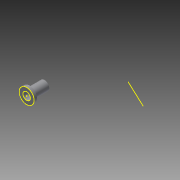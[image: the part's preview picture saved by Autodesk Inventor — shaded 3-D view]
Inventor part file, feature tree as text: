
AUTODESK INVENTOR PART (.ipt)
format: ipt  version: 2013 (Build 170138000, 138)  size: 74,240 bytes
history: native  units: in
note: dims shown in document units (in); Inventor stores cm internally (conversion verified against a paired STEP export)
features: other x2, sketch x1, imported_body x1, reference x1
ambient origin geometry x8: Origin, YZ Plane, XZ Plane, XY Plane, X Axis, Y Axis, Z Axis, Center Point
feature tree (5):
  other  "Boss-Extrude2"
  other  "AM-2235 threaded insert1"
  sketch  "Sketch1"
  imported_body  "Base1"
  reference  "Reference1"
